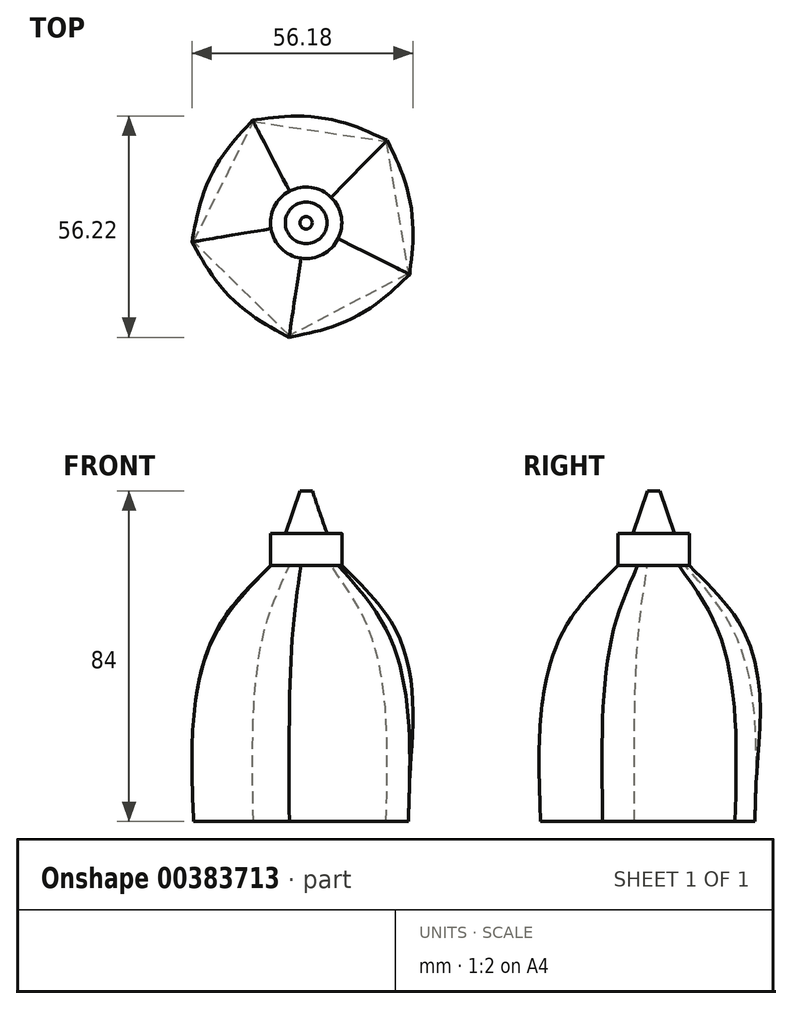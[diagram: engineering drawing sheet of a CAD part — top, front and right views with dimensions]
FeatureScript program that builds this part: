
annotation { "Feature Type Name" : "Feature", "Feature Type Description" : "" }
export const myFeature = defineFeature(function(context is Context, id is Id, definition is map)
    precondition{}
    {
        {
            var Q0;
            Q0=qCreatedBy(makeId("Top.planeOp"),FACE);
            var sketch = newSketch(context, id + "F0", { "sketchPlane" : qUnion([Q0])});
            skCircle(sketch, "E0.cCircle", {"center": v(0, 0) * mm, "radius": 29 * mm, "construction": true});
            skLineSegment(sketch, "E0.0", {"start": v(-4.27, -28.68) * mm, "end": v(-28.6, -4.8) * mm});
            skLineSegment(sketch, "E0.1", {"start": v(-28.6, -4.8) * mm, "end": v(-13.4, 25.71) * mm});
            skLineSegment(sketch, "E0.2", {"start": v(-13.4, 25.71) * mm, "end": v(20.31, 20.7) * mm});
            skLineSegment(sketch, "E0.3", {"start": v(20.31, 20.7) * mm, "end": v(25.96, -12.92) * mm});
            skLineSegment(sketch, "E0.4", {"start": v(25.96, -12.92) * mm, "end": v(-4.27, -28.68) * mm});
            skSolve(sketch);
        }
        {
            var Q0;
            Q0=qCreatedBy(makeId("Top.planeOp"),FACE);
            cPlane(context, id + "F1", {"entities" : qUnion([Q0]), "cplaneType" : CPlaneType.OFFSET, "offset" : 50 * mm, "width" : 150 * mm, "height" : 150 * mm});
        }
        {
            var Q0;
            Q0=qCreatedBy(id+"F1.planeOp",FACE);
            var sketch = newSketch(context, id + "F2", { "sketchPlane" : qUnion([Q0])});
            skCircle(sketch, "E1", {"center": v(0, 0) * mm, "radius": 22.02 * mm});
            skSolve(sketch);
        }
        {
            var Q0;
            Q0=qCreatedBy(makeId("Top.planeOp"),FACE);
            cPlane(context, id + "F3", {"entities" : qUnion([Q0]), "cplaneType" : CPlaneType.OFFSET, "offset" : 65 * mm, "width" : 150 * mm, "height" : 150 * mm});
        }
        {
            var Q0;
            Q0=qCreatedBy(id+"F3.planeOp",FACE);
            var sketch = newSketch(context, id + "F4", { "sketchPlane" : qUnion([Q0])});
            skCircle(sketch, "E2", {"center": v(0, 0) * mm, "radius": 9.07 * mm});
            skSolve(sketch);
        }
        {
            var Q0;
            Q0 = qSketchRegion(id + "F0", true);
            var Q1;
            Q1 = qSketchRegion(id + "F2", true);
            var Q2;
            Q2 = qSketchRegion(id + "F4", true);
            loft(context, id + "F5", {"sheetProfilesArray" : [{ "sheetProfileEntities" : qUnion([Q0]) }, { "sheetProfileEntities" : qUnion([Q1]) }, { "sheetProfileEntities" : qUnion([Q2]) }]});
        }
        {
            var Q0;
            Q0=makeQuery(id+"F5.opLoft","CAP_FACE",FACE,{"disambiguationData":[OSD([makeQuery(id+"F4.imprint","IMPRINT",FACE,{"disambiguationData":[TD([[makeQuery(id+"F4.imprint","IMPRINT",EDGE,{"derivedFrom":sQuery(id+"F4.wireOp",EDGE,"E2")}),1.0]])]})])],"isStart":true});
            extrude(context, id + "F6", {"entities" : qUnion([Q0]), "operationType" : NewBodyOperationType.ADD, "depth" : 8.2 * mm});
        }
        {
            var Q0;
            Q0=qCreatedBy(makeId("Top.planeOp"),FACE);
            cPlane(context, id + "F7", {"entities" : qUnion([Q0]), "cplaneType" : CPlaneType.OFFSET, "offset" : 73 * mm, "width" : 150 * mm, "height" : 150 * mm});
        }
        {
            var Q0;
            Q0=qCreatedBy(id+"F7.planeOp",FACE);
            var sketch = newSketch(context, id + "F8", { "sketchPlane" : qUnion([Q0])});
            skCircle(sketch, "E3", {"center": v(0, 0) * mm, "radius": 5.36 * mm});
            skSolve(sketch);
        }
        {
            var Q0;
            Q0=qCreatedBy(makeId("Top.planeOp"),FACE);
            cPlane(context, id + "F9", {"entities" : qUnion([Q0]), "cplaneType" : CPlaneType.OFFSET, "offset" : 84 * mm, "width" : 150 * mm, "height" : 150 * mm});
        }
        {
            var Q0;
            Q0=qCreatedBy(id+"F9.planeOp",FACE);
            var sketch = newSketch(context, id + "F10", { "sketchPlane" : qUnion([Q0])});
            skCircle(sketch, "E4", {"center": v(0, 0) * mm, "radius": 1.57 * mm});
            skSolve(sketch);
        }
        {
            var Q1;
            Q1 = qSketchRegion(id + "F10", true);
            var Q2;
            Q2 = qSketchRegion(id + "F8", true);
            loft(context, id + "F11", {"operationType" : NewBodyOperationType.ADD, "sheetProfilesArray" : [{ "sheetProfileEntities" : qUnion([Q1]) }, { "sheetProfileEntities" : qUnion([Q2]) }]});
        }
    });
